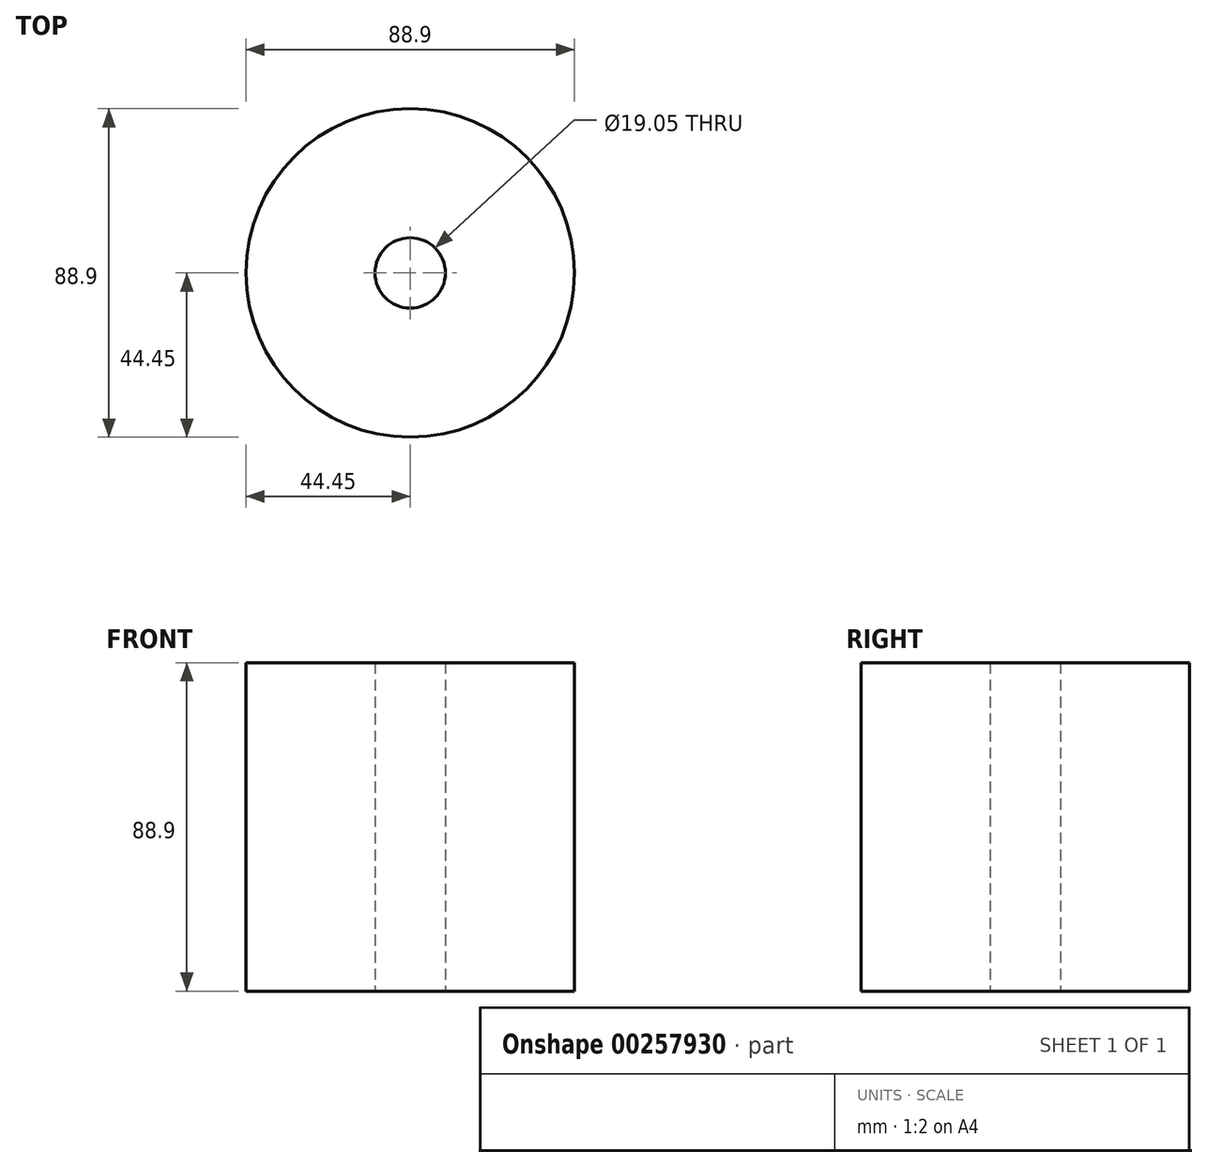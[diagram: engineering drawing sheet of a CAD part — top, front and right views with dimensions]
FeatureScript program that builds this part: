
annotation { "Feature Type Name" : "Feature", "Feature Type Description" : "" }
export const myFeature = defineFeature(function(context is Context, id is Id, definition is map)
    precondition{}
    {
        {
            var Q0;
            Q0=qCreatedBy(makeId("Top.planeOp"),FACE);
            var sketch = newSketch(context, id + "F0", { "sketchPlane" : qUnion([Q0])});
            skCircle(sketch, "E0", {"center": v(0, 0) * mm, "radius": 44.45 * mm});
            skCircle(sketch, "E1", {"center": v(0, 0) * mm, "radius": 25.4 * mm});
            skCircle(sketch, "E2", {"center": v(0, 0) * mm, "radius": 19.05 * mm});
            skCircle(sketch, "E3", {"center": v(0, 0) * mm, "radius": 9.53 * mm});
            skSolve(sketch);
        }
        {
            var Q0;
            Q0=makeQuery(id+"F0.imprint","IMPRINT",FACE,{"disambiguationData":[TD([[makeQuery(id+"F0.imprint","IMPRINT",EDGE,{"derivedFrom":sQuery(id+"F0.wireOp",EDGE,"E0")}),1.0]])]});
            var Q1;
            Q1=makeQuery(id+"F0.imprint","IMPRINT",FACE,{"disambiguationData":[TD([[makeQuery(id+"F0.imprint","IMPRINT",EDGE,{"derivedFrom":sQuery(id+"F0.wireOp",EDGE,"E1")}),1.0]])]});
            var Q2;
            Q2=makeQuery(id+"F0.imprint","IMPRINT",FACE,{"disambiguationData":[TD([[makeQuery(id+"F0.imprint","IMPRINT",EDGE,{"derivedFrom":sQuery(id+"F0.wireOp",EDGE,"E2")}),1.0]])]});
            extrude(context, id + "F1", {"entities" : qUnion([Q0, Q1, Q2]), "depth" : 88.9 * mm});
        }
    });
